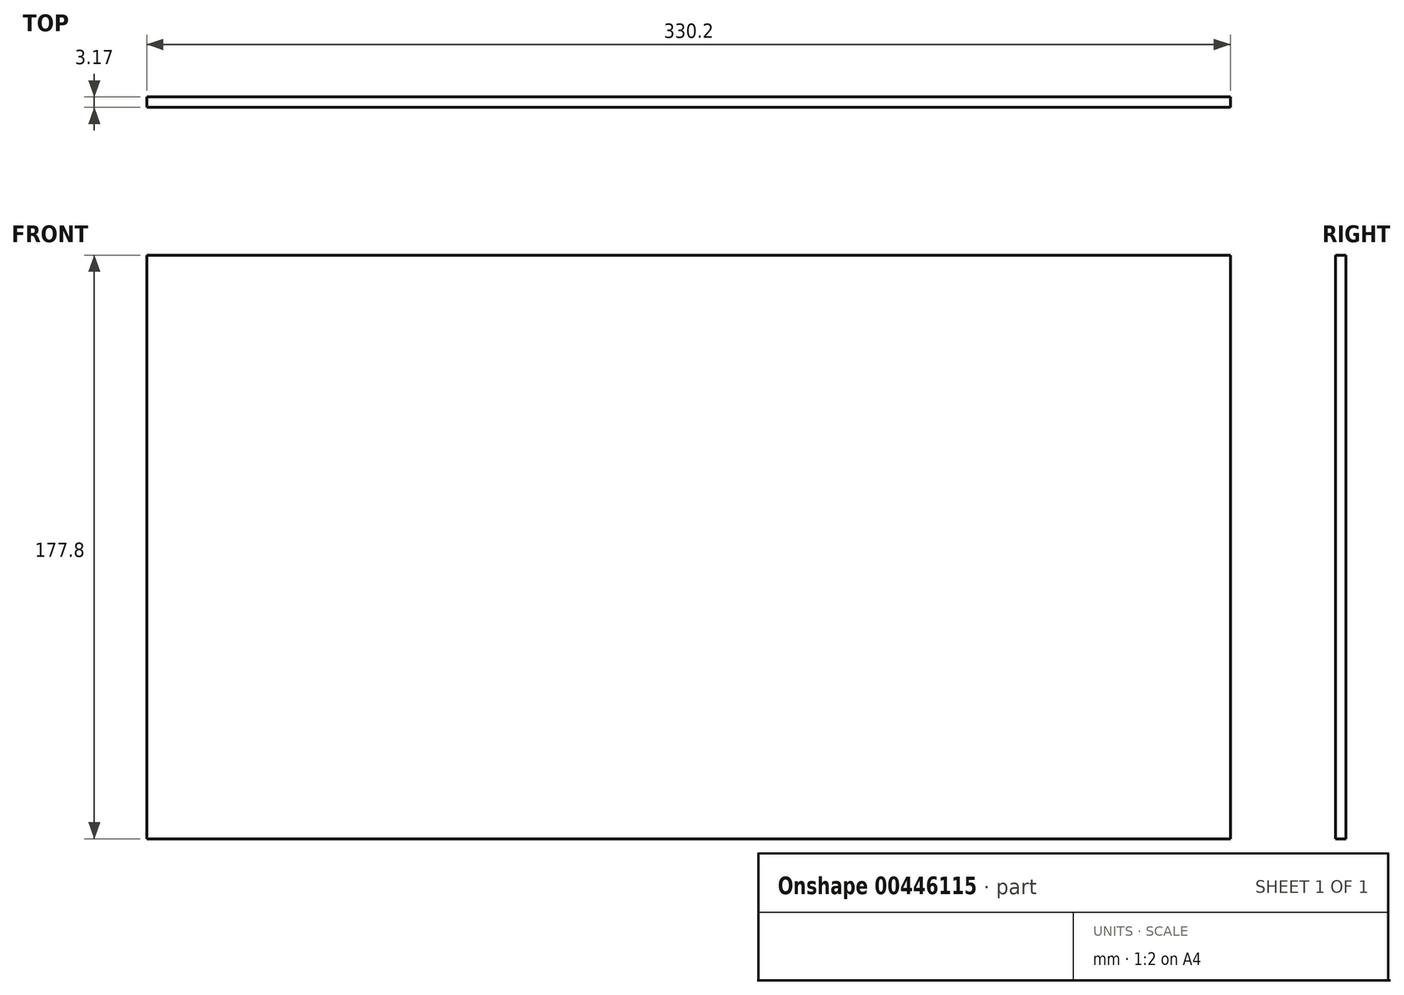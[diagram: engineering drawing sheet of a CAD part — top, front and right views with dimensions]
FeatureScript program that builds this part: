
annotation { "Feature Type Name" : "Feature", "Feature Type Description" : "" }
export const myFeature = defineFeature(function(context is Context, id is Id, definition is map)
    precondition{}
    {
        {
            var Q0;
            Q0=qCreatedBy(makeId("Front.planeOp"),FACE);
            var sketch = newSketch(context, id + "F0", { "sketchPlane" : qUnion([Q0])});
            skLineSegment(sketch, "E0.bottom", {"start": v(185.04, -10.84) * mm, "end": v(-145.16, -10.84) * mm});
            skLineSegment(sketch, "E0.top", {"start": v(185.04, 166.96) * mm, "end": v(-145.16, 166.96) * mm});
            skLineSegment(sketch, "E0.left", {"start": v(185.04, -10.84) * mm, "end": v(185.04, 166.96) * mm});
            skLineSegment(sketch, "E0.right", {"start": v(-145.16, -10.84) * mm, "end": v(-145.16, 166.96) * mm});
            skSolve(sketch);
        }
        {
            var Q0;
            Q0=makeQuery(id+"F0.imprint","IMPRINT",FACE,{"disambiguationData":[TD([[makeQuery(id+"F0.imprint","IMPRINT",EDGE,{"derivedFrom":sQuery(id+"F0.wireOp",EDGE,"E0.bottom")}),-1.0]])]});
            extrude(context, id + "F1", {"entities" : qUnion([Q0]), "depth" : 3.17 * mm});
        }
    });
